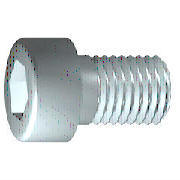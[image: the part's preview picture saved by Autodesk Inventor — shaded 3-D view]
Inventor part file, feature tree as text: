
AUTODESK INVENTOR PART (.ipt)
format: ipt  version: 2022 (Build 260153000, 153)  size: 189,440 bytes
history: native  units: mm (DEFAULTED — no unit token found)
features: sketch x2, other x1, extrude x1, plane x1, fillet x1
ambient origin geometry x7: Origin, YZ Plane, XY Plane, X Axis, Y Axis, Z Axis, Center Point
bodies: Solid1 (feature_tree)
feature tree (6):
  other  "Базовый элемент"
  extrude  "Паз"  Depth=14.65mm
  plane  "Work Plane1"
  fillet  "Fillet2"  Radius=0.276153mm
  sketch  "Эскиз1"
  sketch  "Эскиз2"
